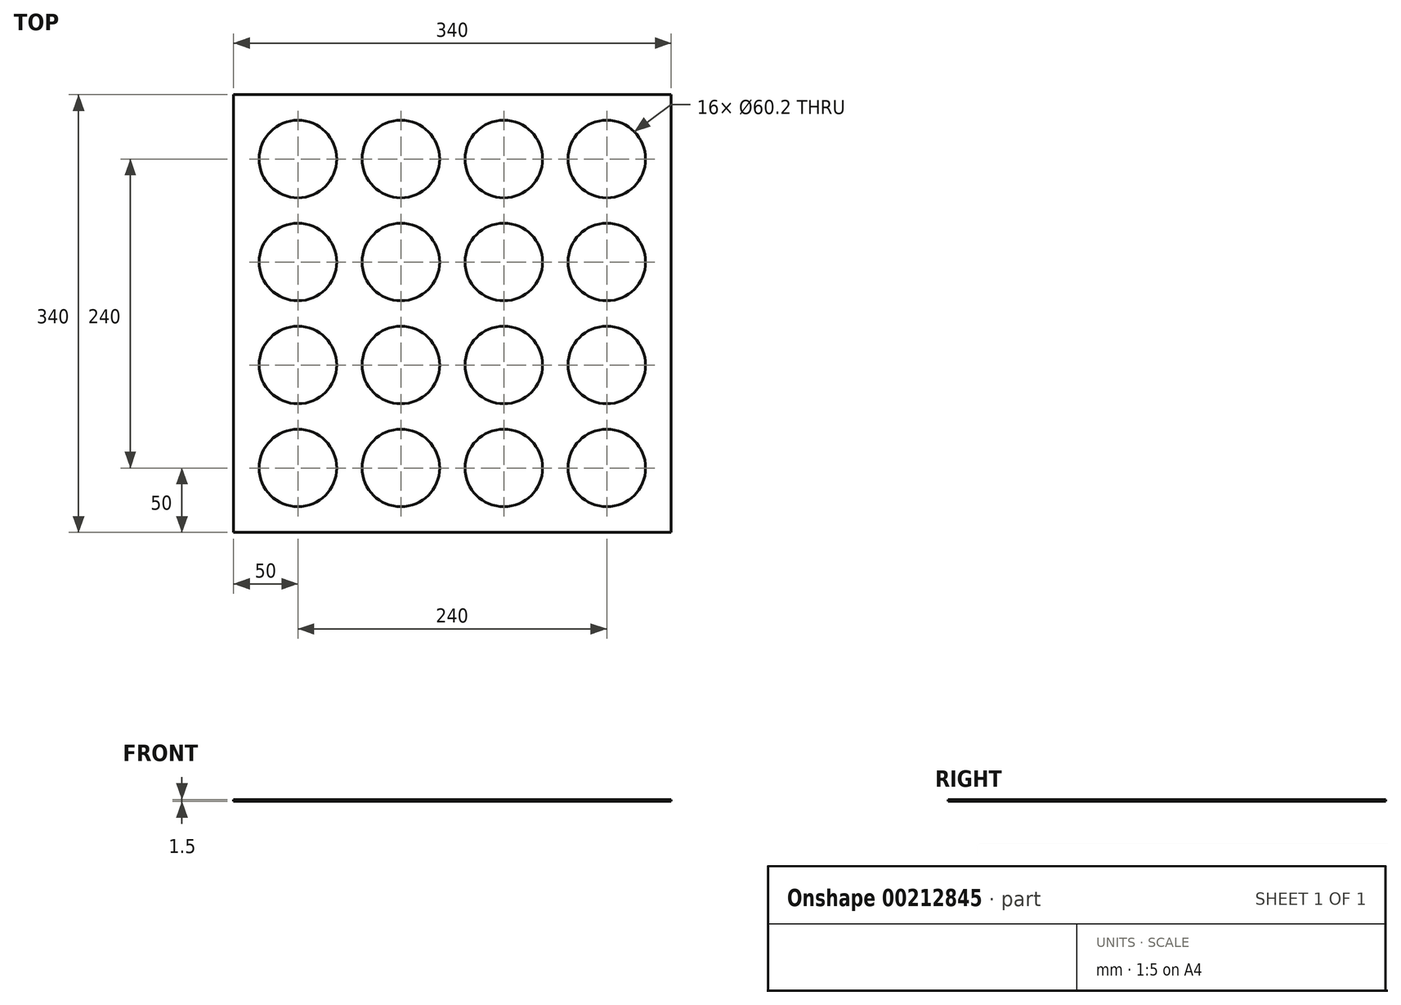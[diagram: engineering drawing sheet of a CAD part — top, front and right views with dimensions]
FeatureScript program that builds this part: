
annotation { "Feature Type Name" : "Feature", "Feature Type Description" : "" }
export const myFeature = defineFeature(function(context is Context, id is Id, definition is map)
    precondition{}
    {
        {
            var Q0;
            Q0=qCreatedBy(makeId("Top.planeOp"),FACE);
            var sketch = newSketch(context, id + "F0", { "sketchPlane" : qUnion([Q0])});
            skLineSegment(sketch, "E0.bottom", {"start": v(-170, 170) * mm, "end": v(170, 170) * mm});
            skLineSegment(sketch, "E0.top", {"start": v(-170, -170) * mm, "end": v(170, -170) * mm});
            skLineSegment(sketch, "E0.left", {"start": v(-170, 170) * mm, "end": v(-170, -170) * mm});
            skLineSegment(sketch, "E0.right", {"start": v(170, 170) * mm, "end": v(170, -170) * mm});
            skCircle(sketch, "E1", {"center": v(-120, 120) * mm, "radius": 30.1 * mm});
            skCircle(sketch, "E2.0.1.0", {"center": v(-120, 40) * mm, "radius": 30.1 * mm});
            skCircle(sketch, "E2.0.2.0", {"center": v(-120, -40) * mm, "radius": 30.1 * mm});
            skCircle(sketch, "E2.0.3.0", {"center": v(-120, -120) * mm, "radius": 30.1 * mm});
            skCircle(sketch, "E2.1.0.0", {"center": v(-40, 120) * mm, "radius": 30.1 * mm});
            skCircle(sketch, "E2.1.1.0", {"center": v(-40, 40) * mm, "radius": 30.1 * mm});
            skCircle(sketch, "E2.1.2.0", {"center": v(-40, -40) * mm, "radius": 30.1 * mm});
            skCircle(sketch, "E2.1.3.0", {"center": v(-40, -120) * mm, "radius": 30.1 * mm});
            skCircle(sketch, "E2.2.0.0", {"center": v(40, 120) * mm, "radius": 30.1 * mm});
            skCircle(sketch, "E2.2.1.0", {"center": v(40, 40) * mm, "radius": 30.1 * mm});
            skCircle(sketch, "E2.2.2.0", {"center": v(40, -40) * mm, "radius": 30.1 * mm});
            skCircle(sketch, "E2.2.3.0", {"center": v(40, -120) * mm, "radius": 30.1 * mm});
            skCircle(sketch, "E2.3.0.0", {"center": v(120, 120) * mm, "radius": 30.1 * mm});
            skCircle(sketch, "E2.3.1.0", {"center": v(120, 40) * mm, "radius": 30.1 * mm});
            skCircle(sketch, "E2.3.2.0", {"center": v(120, -40) * mm, "radius": 30.1 * mm});
            skCircle(sketch, "E2.3.3.0", {"center": v(120, -120) * mm, "radius": 30.1 * mm});
            skLineSegment(sketch, "E2.direction1", {"start": v(-120, 120) * mm, "end": v(-40, 120) * mm, "construction": true});
            skLineSegment(sketch, "E2.direction2", {"start": v(-120, 120) * mm, "end": v(-120, 40) * mm, "construction": true});
            skSolve(sketch);
        }
        {
            var Q0;
            Q0=makeQuery(id+"F0.imprint","IMPRINT",FACE,{"disambiguationData":[TD([[makeQuery(id+"F0.imprint","IMPRINT",EDGE,{"derivedFrom":sQuery(id+"F0.wireOp",EDGE,"E0.bottom")}),-1.0]])]});
            extrude(context, id + "F1", {"entities" : qUnion([Q0]), "depth" : 1.5 * mm});
        }
    });
